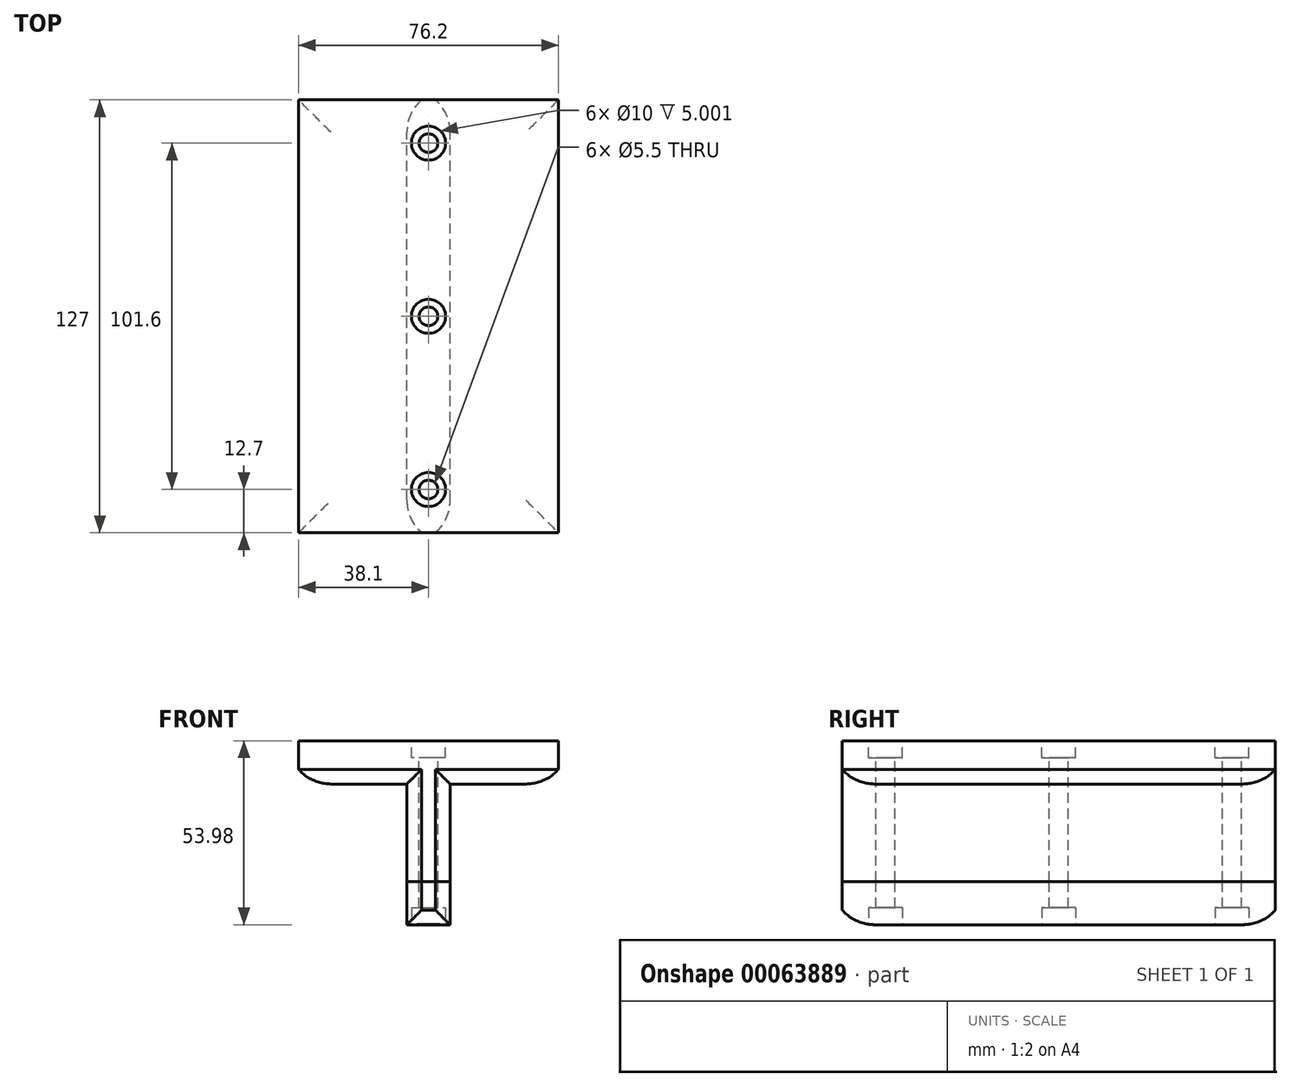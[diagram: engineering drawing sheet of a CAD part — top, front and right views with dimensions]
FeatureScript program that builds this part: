
annotation { "Feature Type Name" : "Feature", "Feature Type Description" : "" }
export const myFeature = defineFeature(function(context is Context, id is Id, definition is map)
    precondition{}
    {
        {
            var Q0;
            Q0=qCreatedBy(makeId("Front.planeOp"),FACE);
            var sketch = newSketch(context, id + "F0", { "sketchPlane" : qUnion([Q0])});
            skLineSegment(sketch, "E0.bottom", {"start": v(-6.35, 22.68) * mm, "end": v(6.35, 22.68) * mm, "construction": true});
            skLineSegment(sketch, "E0.top", {"start": v(-6.35, -5.9) * mm, "end": v(6.35, -5.9) * mm});
            skLineSegment(sketch, "E0.left", {"start": v(-6.35, 22.68) * mm, "end": v(-6.35, -5.9) * mm});
            skLineSegment(sketch, "E0.right", {"start": v(6.35, 22.68) * mm, "end": v(6.35, -5.9) * mm});
            skLineSegment(sketch, "E1.bottom", {"start": v(-38.1, 35.38) * mm, "end": v(38.1, 35.38) * mm});
            skLineSegment(sketch, "E1.left", {"start": v(-38.1, 35.38) * mm, "end": v(-38.1, 22.68) * mm});
            skLineSegment(sketch, "E1.right", {"start": v(38.1, 35.38) * mm, "end": v(38.1, 22.68) * mm});
            skLineSegment(sketch, "E2", {"start": v(-6.35, 22.68) * mm, "end": v(-38.1, 22.68) * mm});
            skLineSegment(sketch, "E3", {"start": v(6.35, 22.68) * mm, "end": v(38.1, 22.68) * mm});
            skLineSegment(sketch, "E4", {"start": v(-38.1, 35.38) * mm, "end": v(6.35, -5.9) * mm, "construction": true});
            skLineSegment(sketch, "E5", {"start": v(-6.35, -5.9) * mm, "end": v(38.1, 35.38) * mm, "construction": true});
            skSolve(sketch);
        }
        {
            var Q0;
            Q0 = qSketchRegion(id + "F0", true);
            extrude(context, id + "F1", {"entities" : qUnion([Q0]), "endBound" : BoundingType.SYMMETRIC, "depth" : 127 * mm});
        }
        {
            var Q0;
            Q0=makeQuery(id+"F1.opExtrude","SWEPT_FACE",FACE,{"disambiguationData":[OSD([sQuery(id+"F0.wireOp",EDGE,"E0.top")])]});
            var sketch = newSketch(context, id + "F2", { "sketchPlane" : qUnion([Q0])});
            skLineSegment(sketch, "E6.bottom", {"start": v(-6.35, 63.5) * mm, "end": v(6.35, 63.5) * mm});
            skLineSegment(sketch, "E6.top", {"start": v(-6.35, -63.5) * mm, "end": v(6.35, -63.5) * mm});
            skLineSegment(sketch, "E6.left", {"start": v(-6.35, 63.5) * mm, "end": v(-6.35, -63.5) * mm});
            skLineSegment(sketch, "E6.right", {"start": v(6.35, 63.5) * mm, "end": v(6.35, -63.5) * mm});
            skSolve(sketch);
        }
        {
            var Q0;
            Q0 = qSketchRegion(id + "F2", true);
            extrude(context, id + "F3", {"entities" : qUnion([Q0]), "depth" : 12.7 * mm});
        }
        {
            var Q0;
            Q0=makeQuery(id+"F1.opExtrude","SWEPT_FACE",FACE,{"disambiguationData":[OSD([sQuery(id+"F0.wireOp",EDGE,"E1.bottom")])]});
            var sketch = newSketch(context, id + "F4", { "sketchPlane" : qUnion([Q0])});
            skLineSegment(sketch, "E7", {"start": v(0, 63.5) * mm, "end": v(0, -63.5) * mm, "construction": true});
            skCircle(sketch, "E8", {"center": v(0, 50.8) * mm, "radius": 5 * mm});
            skCircle(sketch, "E9", {"center": v(0, -50.8) * mm, "radius": 5 * mm});
            skCircle(sketch, "E10", {"center": v(0, 0) * mm, "radius": 5 * mm});
            skLineSegment(sketch, "E11", {"start": v(38.1, 0) * mm, "end": v(-38.1, 0) * mm, "construction": true});
            skSolve(sketch);
        }
        {
            var Q0;
            Q0 = qSketchRegion(id + "F4", true);
            extrude(context, id + "F5", {"entities" : qUnion([Q0]), "operationType" : NewBodyOperationType.REMOVE, "oppositeDirection" : true, "depth" : 5 * mm});
        }
        {
            var Q0;
            Q0=makeQuery(id+"F3.opExtrude","CAP_FACE",FACE,{"disambiguationData":[OSD([sQuery(id+"F2.wireOp",EDGE,"E6.bottom"),sQuery(id+"F2.wireOp",EDGE,"E6.top"),sQuery(id+"F2.wireOp",EDGE,"E6.left"),sQuery(id+"F2.wireOp",EDGE,"E6.right")])],"isStart":false});
            var sketch = newSketch(context, id + "F6", { "sketchPlane" : qUnion([Q0])});
            skCircle(sketch, "E12.0", {"center": v(0, 0) * mm, "radius": 5 * mm});
            skCircle(sketch, "E12.1", {"center": v(0, -50.8) * mm, "radius": 5 * mm});
            skCircle(sketch, "E12.2", {"center": v(0, 50.8) * mm, "radius": 5 * mm});
            skSolve(sketch);
        }
        {
            var Q0;
            Q0 = qSketchRegion(id + "F6", true);
            extrude(context, id + "F7", {"entities" : qUnion([Q0]), "operationType" : NewBodyOperationType.REMOVE, "oppositeDirection" : true, "depth" : 5 * mm});
        }
        {
            var Q0;
            Q0=makeQuery(id+"F5.boolean.opBoolean","COPY",FACE,{"derivedFrom":makeQuery(id+"F5.opExtrude","CAP_FACE",FACE,{"disambiguationData":[OSD([sQuery(id+"F4.wireOp",EDGE,"E10")])],"isStart":false})});
            var sketch = newSketch(context, id + "F8", { "sketchPlane" : qUnion([Q0])});
            skCircle(sketch, "E13", {"center": v(0, 0) * mm, "radius": 2.75 * mm});
            skCircle(sketch, "E14", {"center": v(0, 50.8) * mm, "radius": 2.75 * mm});
            skCircle(sketch, "E15", {"center": v(0, -50.8) * mm, "radius": 2.75 * mm});
            skSolve(sketch);
        }
        {
            var Q0;
            Q0 = qSketchRegion(id + "F8", true);
            extrude(context, id + "F9", {"entities" : qUnion([Q0]), "operationType" : NewBodyOperationType.REMOVE, "endBound" : BoundingType.THROUGH_ALL, "oppositeDirection" : true, "depth" : 50.8 * mm});
        }
        {
            var Q0;
            Q0=makeQuery(id+"F1.opExtrude","SWEPT_FACE",FACE,{"disambiguationData":[OSD([sQuery(id+"F0.wireOp",EDGE,"E1.right")])]});
            var sketch = newSketch(context, id + "F10", { "sketchPlane" : qUnion([Q0])});
            skArc(sketch, "E16", {"start": v(-63.5, 26.98) * mm, "mid": v(-59.2, 23.8) * mm, "end": v(-53.98, 22.68) * mm});
            skLineSegment(sketch, "E17.0", {"start": v(-63.5, 26.98) * mm, "end": v(-63.5, 22.68) * mm});
            skLineSegment(sketch, "E17.1", {"start": v(-63.5, 22.68) * mm, "end": v(-53.98, 22.68) * mm});
            skPoint(sketch, "E18.orphan", {"position": v(-63.5, 35.38) * mm});
            skPoint(sketch, "E19.orphan", {"position": v(63.5, 22.68) * mm});
            skLineSegment(sketch, "E20", {"start": v(0, 35.38) * mm, "end": v(0, -18.6) * mm, "construction": true});
            skPoint(sketch, "E20.endSnap0", {"position": v(0, 35.38) * mm});
            skLineSegment(sketch, "E21.MirrorCS", {"start": v(63.5, 22.68) * mm, "end": v(53.98, 22.68) * mm});
            skLineSegment(sketch, "E22.MirrorCS", {"start": v(63.5, 26.98) * mm, "end": v(63.5, 22.68) * mm});
            skArc(sketch, "E23.MirrorCS", {"start": v(63.5, 26.98) * mm, "mid": v(59.2, 23.8) * mm, "end": v(53.98, 22.68) * mm});
            skSolve(sketch);
        }
        {
            var Q0;
            Q0=makeQuery(id+"F10.imprint","IMPRINT",FACE,{"disambiguationData":[TD([[makeQuery(id+"F10.imprint","IMPRINT",EDGE,{"derivedFrom":sQuery(id+"F10.wireOp",EDGE,"E16")}),-1.0]])]});
            var Q1;
            Q1=makeQuery(id+"F10.imprint","IMPRINT",FACE,{"disambiguationData":[TD([[makeQuery(id+"F10.imprint","IMPRINT",EDGE,{"derivedFrom":sQuery(id+"F10.wireOp",EDGE,"E21.MirrorCS")}),1.0]])]});
            var Q2;
            Q2=makeQuery(id+"F1.opExtrude","CAP_EDGE",EDGE,{"disambiguationData":[OSD([sQuery(id+"F0.wireOp",EDGE,"E3")])],"isStart":false});
            var Q3;
            Q3=makeQuery(id+"F1.opExtrude","CAP_EDGE",EDGE,{"disambiguationData":[OSD([sQuery(id+"F0.wireOp",EDGE,"E0.right")])],"isStart":false});
            sweep(context, id + "F11", {"operationType" : NewBodyOperationType.REMOVE, "profiles" : qUnion([Q0, Q1]), "path" : qUnion([Q2, Q3])});
        }
        {
            var Q0;
            Q0=makeQuery(id+"F1.opExtrude","SWEPT_FACE",FACE,{"disambiguationData":[OSD([sQuery(id+"F0.wireOp",EDGE,"E1.left")])]});
            var sketch = newSketch(context, id + "F12", { "sketchPlane" : qUnion([Q0])});
            skLineSegment(sketch, "E24.0", {"start": v(63.5, 22.68) * mm, "end": v(53.98, 22.68) * mm});
            skArc(sketch, "E24.1", {"start": v(63.5, 26.98) * mm, "mid": v(59.2, 23.8) * mm, "end": v(53.98, 22.68) * mm});
            skLineSegment(sketch, "E24.2", {"start": v(63.5, 26.98) * mm, "end": v(63.5, 22.68) * mm});
            skLineSegment(sketch, "E25.0", {"start": v(-63.5, 22.68) * mm, "end": v(-53.98, 22.68) * mm});
            skArc(sketch, "E25.1", {"start": v(-63.5, 26.98) * mm, "mid": v(-59.2, 23.8) * mm, "end": v(-53.98, 22.68) * mm});
            skLineSegment(sketch, "E25.2", {"start": v(-63.5, 26.98) * mm, "end": v(-63.5, 22.68) * mm});
            skSolve(sketch);
        }
        {
            var Q0;
            Q0 = qSketchRegion(id + "F12", true);
            var Q1;
            Q1=makeQuery(id+"F1.opExtrude","CAP_EDGE",EDGE,{"disambiguationData":[OSD([sQuery(id+"F0.wireOp",EDGE,"E2")])],"isStart":false});
            var Q2;
            Q2=makeQuery(id+"F1.opExtrude","CAP_EDGE",EDGE,{"disambiguationData":[OSD([sQuery(id+"F0.wireOp",EDGE,"E0.left")])],"isStart":false});
            sweep(context, id + "F13", {"operationType" : NewBodyOperationType.REMOVE, "profiles" : qUnion([Q0]), "path" : qUnion([Q1, Q2])});
        }
        {
            var Q0;
            Q0=makeQuery(id+"F3.opExtrude","CAP_FACE",FACE,{"disambiguationData":[OSD([sQuery(id+"F2.wireOp",EDGE,"E6.bottom"),sQuery(id+"F2.wireOp",EDGE,"E6.top"),sQuery(id+"F2.wireOp",EDGE,"E6.left"),sQuery(id+"F2.wireOp",EDGE,"E6.right")])],"isStart":true});
            var sketch = newSketch(context, id + "F14", { "sketchPlane" : qUnion([Q0])});
            skArc(sketch, "E26.0", {"start": v(-6.35, 53.97) * mm, "mid": v(-5.23, 59.2) * mm, "end": v(-2.05, 63.5) * mm});
            skLineSegment(sketch, "E26.1", {"start": v(-6.35, -63.5) * mm, "end": v(-6.35, -53.98) * mm});
            skLineSegment(sketch, "E26.2", {"start": v(-6.35, 63.5) * mm, "end": v(-2.05, 63.5) * mm});
            skLineSegment(sketch, "E26.3", {"start": v(6.35, -63.5) * mm, "end": v(6.35, -53.97) * mm});
            skArc(sketch, "E26.4", {"start": v(2.05, 63.5) * mm, "mid": v(5.23, 59.2) * mm, "end": v(6.35, 53.98) * mm});
            skArc(sketch, "E26.5", {"start": v(-2.05, -63.5) * mm, "mid": v(-5.23, -59.2) * mm, "end": v(-6.35, -53.98) * mm});
            skLineSegment(sketch, "E26.6", {"start": v(-6.35, -63.5) * mm, "end": v(-2.05, -63.5) * mm});
            skArc(sketch, "E26.7", {"start": v(6.35, -53.97) * mm, "mid": v(5.23, -59.2) * mm, "end": v(2.05, -63.5) * mm});
            skLineSegment(sketch, "E27.trimOffspring", {"start": v(2.05, -63.5) * mm, "end": v(6.35, -63.5) * mm});
            skLineSegment(sketch, "E28.trimOffspring", {"start": v(-6.35, 53.97) * mm, "end": v(-6.35, 63.5) * mm});
            skLineSegment(sketch, "E29.trimOffspring", {"start": v(6.35, 53.97) * mm, "end": v(6.35, 63.5) * mm});
            skLineSegment(sketch, "E30.trimOffspring", {"start": v(2.05, 63.5) * mm, "end": v(6.35, 63.5) * mm});
            skSolve(sketch);
        }
        {
            var Q0;
            Q0 = qSketchRegion(id + "F14", true);
            extrude(context, id + "F15", {"entities" : qUnion([Q0]), "operationType" : NewBodyOperationType.REMOVE, "oppositeDirection" : true, "depth" : 25.4 * mm});
        }
        {
            var Q0;
            Q0=makeQuery(id+"F1.opExtrude","CAP_FACE",FACE,{"disambiguationData":[OSD([sQuery(id+"F0.wireOp",EDGE,"E0.top"),sQuery(id+"F0.wireOp",EDGE,"E0.left"),sQuery(id+"F0.wireOp",EDGE,"E0.right"),sQuery(id+"F0.wireOp",EDGE,"E1.bottom"),sQuery(id+"F0.wireOp",EDGE,"E1.left"),sQuery(id+"F0.wireOp",EDGE,"E1.right"),sQuery(id+"F0.wireOp",EDGE,"E2"),sQuery(id+"F0.wireOp",EDGE,"E3")])],"isStart":true});
            var sketch = newSketch(context, id + "F16", { "sketchPlane" : qUnion([Q0])});
            skArc(sketch, "E31", {"start": v(28.57, 22.68) * mm, "mid": v(33.8, 23.8) * mm, "end": v(38.1, 26.98) * mm});
            skLineSegment(sketch, "E32.0", {"start": v(38.1, 22.68) * mm, "end": v(38.1, 26.98) * mm});
            skLineSegment(sketch, "E32.1", {"start": v(38.1, 22.68) * mm, "end": v(28.57, 22.68) * mm});
            skPoint(sketch, "E33.orphan", {"position": v(6.35, 22.68) * mm});
            skLineSegment(sketch, "E34", {"start": v(0, 35.38) * mm, "end": v(0, -5.9) * mm, "construction": true});
            skLineSegment(sketch, "E35.MirrorCS", {"start": v(-38.1, 22.68) * mm, "end": v(-38.1, 26.98) * mm});
            skLineSegment(sketch, "E36.MirrorCS", {"start": v(-38.1, 22.68) * mm, "end": v(-28.57, 22.68) * mm});
            skArc(sketch, "E37.MirrorCS", {"start": v(-28.57, 22.68) * mm, "mid": v(-33.8, 23.8) * mm, "end": v(-38.1, 26.98) * mm});
            skSolve(sketch);
        }
        {
            var Q0;
            Q0=makeQuery(id+"F16.imprint","IMPRINT",FACE,{"disambiguationData":[TD([[makeQuery(id+"F16.imprint","IMPRINT",EDGE,{"derivedFrom":sQuery(id+"F16.wireOp",EDGE,"E35.MirrorCS")}),-1.0]])]});
            var Q1;
            Q1=makeQuery(id+"F16.imprint","IMPRINT",FACE,{"disambiguationData":[TD([[makeQuery(id+"F16.imprint","IMPRINT",EDGE,{"derivedFrom":sQuery(id+"F16.wireOp",EDGE,"E31")}),-1.0]])]});
            extrude(context, id + "F17", {"entities" : qUnion([Q0, Q1]), "operationType" : NewBodyOperationType.REMOVE, "endBound" : BoundingType.THROUGH_ALL, "oppositeDirection" : true, "depth" : 25.4 * mm});
        }
        {
            var Q0;
            Q0=makeQuery(id+"F3.opExtrude","SWEPT_FACE",FACE,{"disambiguationData":[OSD([sQuery(id+"F2.wireOp",EDGE,"E6.right")])]});
            var sketch = newSketch(context, id + "F18", { "sketchPlane" : qUnion([Q0])});
            skArc(sketch, "E38", {"start": v(-63.5, -14.3) * mm, "mid": v(-59.2, -17.47) * mm, "end": v(-53.98, -18.6) * mm});
            skLineSegment(sketch, "E39.0", {"start": v(-63.5, -18.6) * mm, "end": v(-63.5, -14.3) * mm});
            skLineSegment(sketch, "E39.1", {"start": v(-63.5, -18.6) * mm, "end": v(-53.98, -18.6) * mm});
            skLineSegment(sketch, "E40", {"start": v(0, -18.6) * mm, "end": v(0, 0) * mm, "construction": true});
            skArc(sketch, "E41.MirrorCS", {"start": v(63.5, -14.3) * mm, "mid": v(59.2, -17.47) * mm, "end": v(53.98, -18.6) * mm});
            skLineSegment(sketch, "E42.MirrorCS", {"start": v(63.5, -18.6) * mm, "end": v(53.98, -18.6) * mm});
            skLineSegment(sketch, "E43.MirrorCS", {"start": v(63.5, -18.6) * mm, "end": v(63.5, -14.3) * mm});
            skSolve(sketch);
        }
        {
            var Q0;
            Q0 = qSketchRegion(id + "F18", true);
            extrude(context, id + "F19", {"entities" : qUnion([Q0]), "operationType" : NewBodyOperationType.REMOVE, "endBound" : BoundingType.THROUGH_ALL, "oppositeDirection" : true, "depth" : 25.4 * mm});
        }
    });
